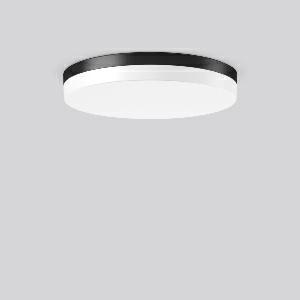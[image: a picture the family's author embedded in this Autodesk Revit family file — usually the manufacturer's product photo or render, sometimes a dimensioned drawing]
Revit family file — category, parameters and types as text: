
# Revit family: flat_slim_round_312634_0031_76_9a6a
name_source: partatom
category: Lighting Fixtures
units: mm (PartAtom-declared; Revit-internal decimal feet)

## family parameters
Cut with Voids When Loaded = No
Host = Face
Light Source = No
Part Type = Normal
Room Calculation Point = No
Round Connector Dimension = Use Diameter
Shared = No

## types (1)
- MultiLumen 1 830 (1 x LED Modul 830, 3450 lm, 3000)
    Apparent Load = 26 VA
    CIE Flux Codes = 40 71 90 84 100
    Color Rendering = 80
    Color Temperature = 3000
    Default Elevation = 1800 mm
    Height = 70 mm
    Lamp = 1 x LED Modul 830
    Lamp Light Flux = 3450 lm
    Lamp count = 1
    Length = 480 mm
    Lifetime = 50000 h
    Luminous efficacy = 133 lm/W
    Manufacturer = RZB
    ModVariant = No
    Model = 312634.0031.76
    Mounting Place = Ceiling
    Mounting Type = Surface mounted
    Number of Poles = 1
    OnlyDefault = Yes
    Power Factor = 1
    Product Name = FLAT SLIM round
    Product group = Surface mounted ceiling and wall luminaires
    ProductGroupID = 305
    Protection Class = Protection class I
    Protection Degree = Degree of protection
    RLX_Detail_Level = 1
    RLX_Emergency_Light_Flux = 0 lm
    RLX_Emergency_Type = 0
    RLX_Emergency_Type_DB = No
    RlxData = <blob elided: 22949 chars, md5=128f427a>
    Socket = socket
    Standby Power = 0 W
    System Light Flux = 3450 lm
    System Power = 26 W
    Type Comments = MultiLumen 1 830
    Type Image = 312633.0031.jpg
    URL = http://relux.com
    VarID = multilumen_1_830
    Voltage = 0 V
    Weight = 0.00 kg
    Width = 0 mm  [stored 0 ft]

note: [stored X ft] marks values corroborated as IEEE doubles in the binary element streams (Revit-internal decimal feet)

## geometry (parser evidence)
native form markers: Blend x4, Sweep x12
no freeform markers — native parametric forms only
